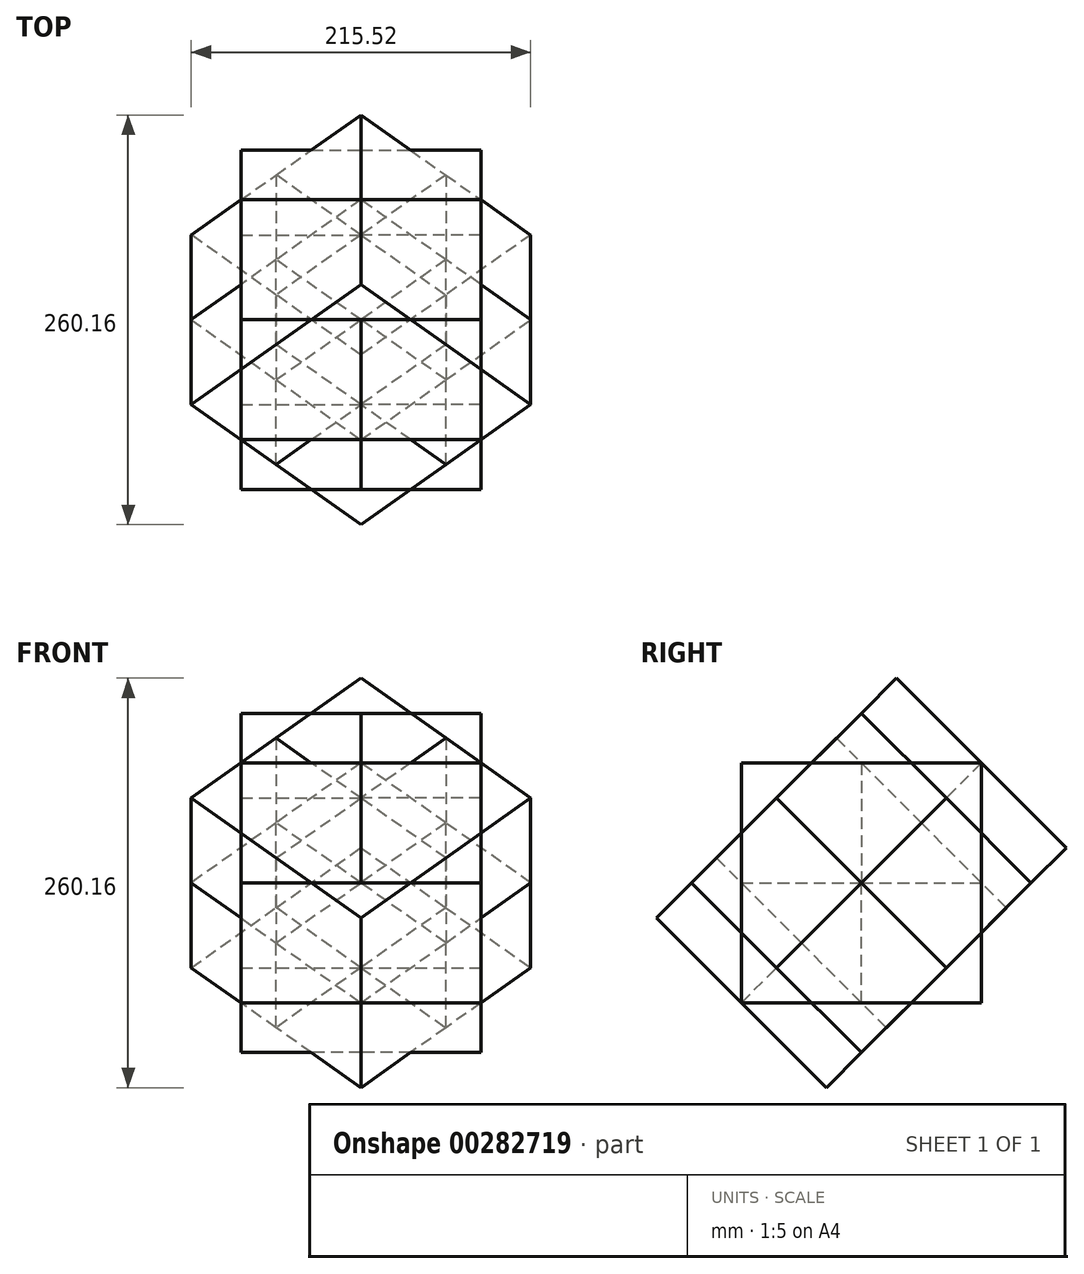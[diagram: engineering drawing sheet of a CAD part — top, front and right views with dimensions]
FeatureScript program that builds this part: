
annotation { "Feature Type Name" : "Feature", "Feature Type Description" : "" }
export const myFeature = defineFeature(function(context is Context, id is Id, definition is map)
    precondition{}
    {
        {
            var Q0;
            Q0=qCreatedBy(makeId("Top.planeOp"),FACE);
            var sketch = newSketch(context, id + "F0", { "sketchPlane" : qUnion([Q0])});
            skLineSegment(sketch, "E0.bottom", {"start": v(0, 0) * mm, "end": v(76.2, 0) * mm});
            skLineSegment(sketch, "E0.top", {"start": v(0, 76.2) * mm, "end": v(76.2, 76.2) * mm});
            skLineSegment(sketch, "E0.left", {"start": v(0, 0) * mm, "end": v(0, 76.2) * mm});
            skLineSegment(sketch, "E0.right", {"start": v(76.2, 0) * mm, "end": v(76.2, 76.2) * mm});
            skSolve(sketch);
        }
        {
            var Q0;
            Q0 = qSketchRegion(id + "F0", true);
            extrude(context, id + "F1", {"entities" : qUnion([Q0]), "depth" : 76.2 * mm});
        }
        {
            var Q0;
            Q0=makeQuery(id+"F1.opExtrude","SWEPT_BODY",BODY,{"disambiguationData":[OSD([sQuery(id+"F0.wireOp",EDGE,"E0.bottom"),sQuery(id+"F0.wireOp",EDGE,"E0.top"),sQuery(id+"F0.wireOp",EDGE,"E0.left"),sQuery(id+"F0.wireOp",EDGE,"E0.right")])]});
            var Q1;
            Q1=makeQuery(id+"F1.opExtrude","CAP_EDGE",EDGE,{"disambiguationData":[OSD([sQuery(id+"F0.wireOp",EDGE,"E0.bottom")])],"isStart":true});
            circularPattern(context, id + "F2", {"entities" : qUnion([Q0]), "axis" : qUnion([Q1]), "angle" : 360 * degree, "instanceCount" : 8, "equalSpace" : true});
        }
        {
            var Q0;
            Q0=makeQuery(id+"F2.opPattern","COPY",BODY,{"derivedFrom":makeQuery(id+"F1.opExtrude","SWEPT_BODY",BODY,{"disambiguationData":[OSD([sQuery(id+"F0.wireOp",EDGE,"E0.bottom"),sQuery(id+"F0.wireOp",EDGE,"E0.top"),sQuery(id+"F0.wireOp",EDGE,"E0.left"),sQuery(id+"F0.wireOp",EDGE,"E0.right")])]}),"instanceName":"1"});
            var Q1;
            Q1=makeQuery(id+"F2.opPattern","COPY",BODY,{"derivedFrom":makeQuery(id+"F1.opExtrude","SWEPT_BODY",BODY,{"disambiguationData":[OSD([sQuery(id+"F0.wireOp",EDGE,"E0.bottom"),sQuery(id+"F0.wireOp",EDGE,"E0.top"),sQuery(id+"F0.wireOp",EDGE,"E0.left"),sQuery(id+"F0.wireOp",EDGE,"E0.right")])]}),"instanceName":"7"});
            var Q2;
            Q2=makeQuery(id+"F2.opPattern","COPY",BODY,{"derivedFrom":makeQuery(id+"F1.opExtrude","SWEPT_BODY",BODY,{"disambiguationData":[OSD([sQuery(id+"F0.wireOp",EDGE,"E0.bottom"),sQuery(id+"F0.wireOp",EDGE,"E0.top"),sQuery(id+"F0.wireOp",EDGE,"E0.left"),sQuery(id+"F0.wireOp",EDGE,"E0.right")])]}),"instanceName":"6"});
            var Q3;
            Q3=makeQuery(id+"F2.opPattern","COPY",BODY,{"derivedFrom":makeQuery(id+"F1.opExtrude","SWEPT_BODY",BODY,{"disambiguationData":[OSD([sQuery(id+"F0.wireOp",EDGE,"E0.bottom"),sQuery(id+"F0.wireOp",EDGE,"E0.top"),sQuery(id+"F0.wireOp",EDGE,"E0.left"),sQuery(id+"F0.wireOp",EDGE,"E0.right")])]}),"instanceName":"2"});
            var Q4;
            Q4=makeQuery(id+"F2.opPattern","COPY",BODY,{"derivedFrom":makeQuery(id+"F1.opExtrude","SWEPT_BODY",BODY,{"disambiguationData":[OSD([sQuery(id+"F0.wireOp",EDGE,"E0.bottom"),sQuery(id+"F0.wireOp",EDGE,"E0.top"),sQuery(id+"F0.wireOp",EDGE,"E0.left"),sQuery(id+"F0.wireOp",EDGE,"E0.right")])]}),"instanceName":"3"});
            var Q5;
            Q5=makeQuery(id+"F1.opExtrude","SWEPT_BODY",BODY,{"disambiguationData":[OSD([sQuery(id+"F0.wireOp",EDGE,"E0.bottom"),sQuery(id+"F0.wireOp",EDGE,"E0.top"),sQuery(id+"F0.wireOp",EDGE,"E0.left"),sQuery(id+"F0.wireOp",EDGE,"E0.right")])]});
            var Q6;
            Q6=makeQuery(id+"F2.opPattern","COPY",BODY,{"derivedFrom":makeQuery(id+"F1.opExtrude","SWEPT_BODY",BODY,{"disambiguationData":[OSD([sQuery(id+"F0.wireOp",EDGE,"E0.bottom"),sQuery(id+"F0.wireOp",EDGE,"E0.top"),sQuery(id+"F0.wireOp",EDGE,"E0.left"),sQuery(id+"F0.wireOp",EDGE,"E0.right")])]}),"instanceName":"5"});
            var Q7;
            Q7=makeQuery(id+"F2.opPattern","COPY",BODY,{"derivedFrom":makeQuery(id+"F1.opExtrude","SWEPT_BODY",BODY,{"disambiguationData":[OSD([sQuery(id+"F0.wireOp",EDGE,"E0.bottom"),sQuery(id+"F0.wireOp",EDGE,"E0.top"),sQuery(id+"F0.wireOp",EDGE,"E0.left"),sQuery(id+"F0.wireOp",EDGE,"E0.right")])]}),"instanceName":"4"});
            var Q8;
            Q8=makeQuery(id+"F2.opPattern","COPY",EDGE,{"derivedFrom":makeQuery(id+"F1.opExtrude","CAP_EDGE",EDGE,{"disambiguationData":[OSD([sQuery(id+"F0.wireOp",EDGE,"E0.right")])],"isStart":true}),"instanceName":"1"});
            circularPattern(context, id + "F3", {"entities" : qUnion([Q0, Q1, Q2, Q3, Q4, Q5, Q6, Q7]), "axis" : qUnion([Q8]), "angle" : 360 * degree, "instanceCount" : 4, "equalSpace" : true});
        }
    });
